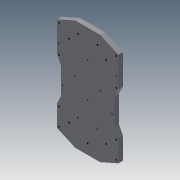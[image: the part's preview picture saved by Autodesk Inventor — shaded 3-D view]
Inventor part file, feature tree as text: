
AUTODESK INVENTOR PART (.ipt)
format: ipt  version: 2013 (Build 170138000, 138)  size: 279,552 bytes
history: native  units: mm
features: extrude x5, sketch x5
ambient origin geometry x8: Origin, YZ Plane, XZ Plane, XY Plane, X Axis, Y Axis, Z Axis, Center Point
bodies: Solid1 (feature_tree)
feature tree (10):
  extrude  "Extrusion1"  Depth=4.0mm
  extrude  "Extrusion2"  Depth=4.0mm
  extrude  "Extrusion3"  Depth=4.0mm
  extrude  "Extrusion4"  Depth=4.0mm
  extrude  "Extrusion5"  Depth=4.0mm
  sketch  "Sketch1"  dims[d0=4.0mm d1=4.0mm]
  sketch  "Sketch2"  dims[d2=4.0mm d3=4.0mm]
  sketch  "Sketch3"  dims[d4=4.0mm d5=4.0mm]
  sketch  "Sketch4"  dims[d6=4.0mm d7=4.0mm]
  sketch  "Sketch5"  dims[d8=4.0mm d9=4.0mm d10=4.0mm d11=4.0mm d12=4.0mm d13=4.0mm d14=4.0mm d15=4.0mm d16=4.0mm d17=4.0mm d18=4.0mm d19=4.0mm d20=4.0mm d21=4.0mm d22=4.0mm d23=4.0mm d24=4.0mm d25=2.0mm d26=0.0mm d27=1.3mm d28=0.0mm d29=8.0mm d30=0.0mm d31=10.0mm d32=0.0mm d33=10.0mm d34=0.0mm]
